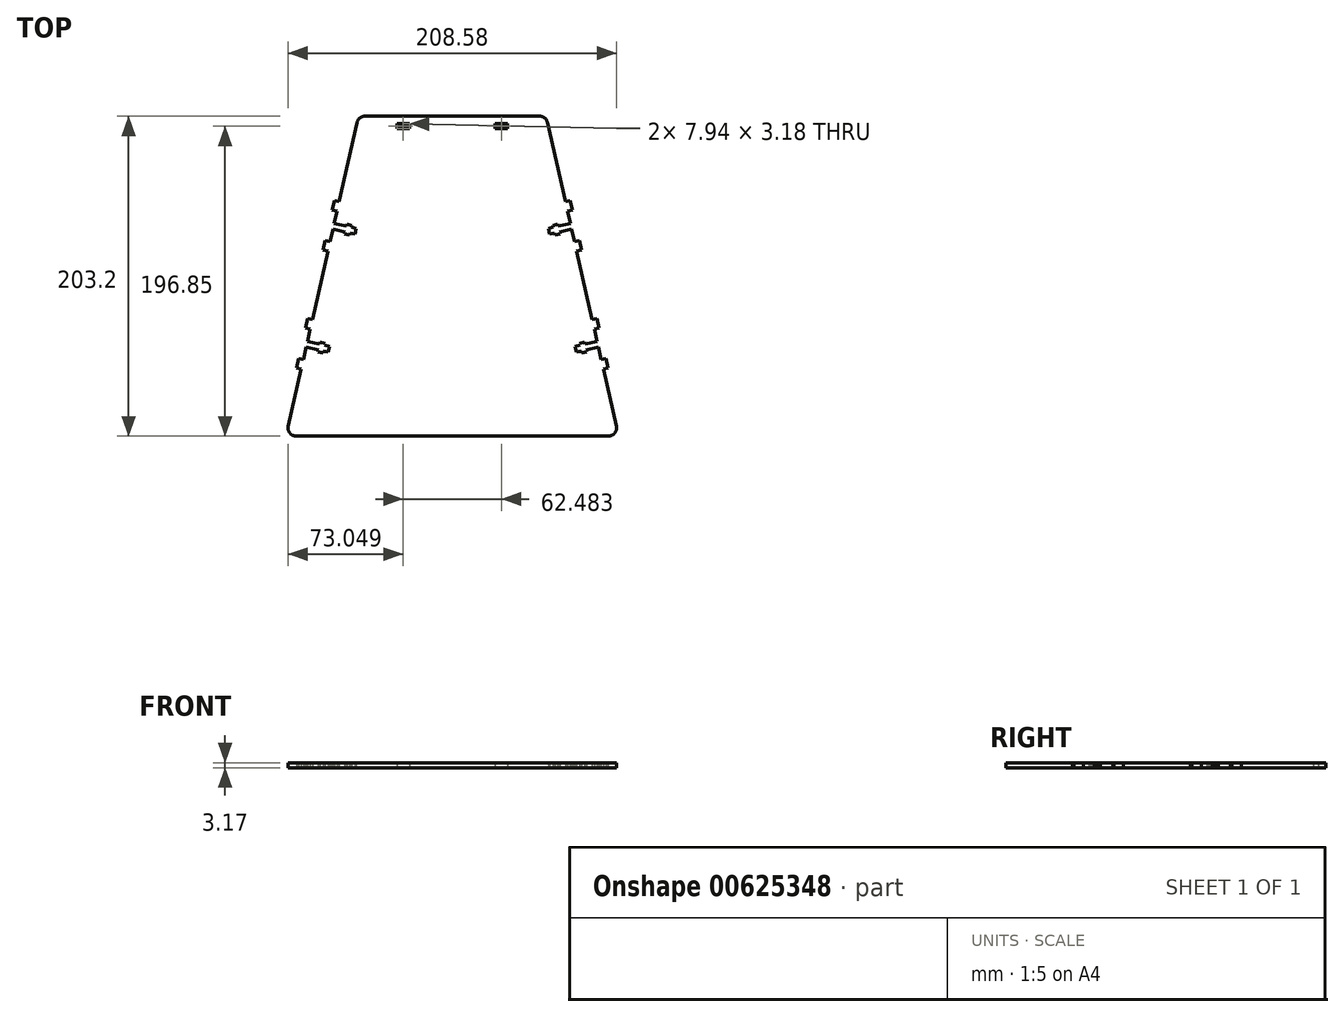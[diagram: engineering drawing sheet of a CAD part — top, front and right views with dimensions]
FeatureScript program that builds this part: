
annotation { "Feature Type Name" : "Feature", "Feature Type Description" : "" }
export const myFeature = defineFeature(function(context is Context, id is Id, definition is map)
    precondition{}
    {
        {
            var Q0;
            Q0=qCreatedBy(makeId("Top.planeOp"),FACE);
            var sketch = newSketch(context, id + "F0", { "sketchPlane" : qUnion([Q0])});
            skLineSegment(sketch, "E0", {"start": v(-59.53, 101.6) * mm, "end": v(59.53, 101.6) * mm});
            skLineSegment(sketch, "E1", {"start": v(-105.57, -101.6) * mm, "end": v(105.57, -101.6) * mm});
            skLineSegment(sketch, "E2", {"start": v(105.57, -101.6) * mm, "end": v(59.53, 101.6) * mm, "construction": true});
            skLineSegment(sketch, "E3", {"start": v(-59.53, 101.6) * mm, "end": v(-105.57, -101.6) * mm, "construction": true});
            skLineSegment(sketch, "E4", {"start": v(0, 0) * mm, "end": v(0, 101.6) * mm, "construction": true});
            skLineSegment(sketch, "E5.bottom", {"start": v(-27.27, 93.66) * mm, "end": v(-35.21, 93.66) * mm});
            skLineSegment(sketch, "E5.top", {"start": v(-27.27, 96.84) * mm, "end": v(-35.21, 96.84) * mm});
            skLineSegment(sketch, "E5.left", {"start": v(-27.27, 93.66) * mm, "end": v(-27.27, 96.84) * mm});
            skLineSegment(sketch, "E5.right", {"start": v(-35.21, 93.66) * mm, "end": v(-35.21, 96.84) * mm});
            skPoint(sketch, "E5.middle", {"position": v(-31.24, 95.25) * mm});
            skLineSegment(sketch, "E6", {"start": v(-35.21, 96.84) * mm, "end": v(-60.61, 96.84) * mm, "construction": true});
            skLineSegment(sketch, "E7", {"start": v(-59.53, 101.6) * mm, "end": v(-71.8, 47.41) * mm});
            skLineSegment(sketch, "E8", {"start": v(-71.8, 47.41) * mm, "end": v(-74.9, 48.11) * mm});
            skLineSegment(sketch, "E9", {"start": v(-74.9, 48.11) * mm, "end": v(-76.3, 41.92) * mm});
            skLineSegment(sketch, "E10", {"start": v(-76.3, 41.92) * mm, "end": v(-73.21, 41.22) * mm});
            skLineSegment(sketch, "E11", {"start": v(-73.21, 41.22) * mm, "end": v(-74.97, 33.48) * mm});
            skLineSegment(sketch, "E12", {"start": v(-74.97, 33.48) * mm, "end": v(-67.22, 31.72) * mm});
            skLineSegment(sketch, "E13", {"start": v(-67.22, 31.72) * mm, "end": v(-66.94, 32.96) * mm});
            skLineSegment(sketch, "E14", {"start": v(-66.94, 32.96) * mm, "end": v(-63.85, 32.26) * mm});
            skLineSegment(sketch, "E15", {"start": v(-63.85, 32.26) * mm, "end": v(-64.13, 31.02) * mm});
            skLineSegment(sketch, "E16", {"start": v(-64.13, 31.02) * mm, "end": v(-61.03, 30.32) * mm});
            skLineSegment(sketch, "E17", {"start": v(-61.03, 30.32) * mm, "end": v(-61.87, 26.6) * mm});
            skLineSegment(sketch, "E18", {"start": v(-61.87, 26.6) * mm, "end": v(-64.97, 27.3) * mm});
            skLineSegment(sketch, "E19", {"start": v(-64.97, 27.3) * mm, "end": v(-65.25, 26.07) * mm});
            skLineSegment(sketch, "E20", {"start": v(-65.25, 26.07) * mm, "end": v(-68.35, 26.77) * mm});
            skLineSegment(sketch, "E21", {"start": v(-68.35, 26.77) * mm, "end": v(-68.07, 28) * mm});
            skLineSegment(sketch, "E22", {"start": v(-68.07, 28) * mm, "end": v(-75.8, 29.76) * mm});
            skLineSegment(sketch, "E23", {"start": v(-75.8, 29.76) * mm, "end": v(-77.56, 22.02) * mm});
            skLineSegment(sketch, "E24", {"start": v(-77.56, 22.02) * mm, "end": v(-80.66, 22.72) * mm});
            skLineSegment(sketch, "E25", {"start": v(-80.66, 22.72) * mm, "end": v(-82.06, 16.53) * mm});
            skLineSegment(sketch, "E26", {"start": v(-82.06, 16.53) * mm, "end": v(-78.96, 15.83) * mm});
            skLineSegment(sketch, "E27", {"start": v(-78.96, 15.83) * mm, "end": v(-88.79, -27.52) * mm});
            skLineSegment(sketch, "E28", {"start": v(-83.88, -5.85) * mm, "end": v(0, -24.85) * mm, "construction": true});
            skLineSegment(sketch, "E29.MirrorCS", {"start": v(-85.04, -46.93) * mm, "end": v(-85.32, -48.17) * mm});
            skLineSegment(sketch, "E30.MirrorCS", {"start": v(-82.23, -48.87) * mm, "end": v(-81.95, -47.63) * mm});
            skLineSegment(sketch, "E31.MirrorCS", {"start": v(-81.1, -43.91) * mm, "end": v(-80.82, -42.68) * mm});
            skLineSegment(sketch, "E32.MirrorCS", {"start": v(-78, -44.62) * mm, "end": v(-81.1, -43.91) * mm});
            skLineSegment(sketch, "E33.MirrorCS", {"start": v(-85.32, -48.17) * mm, "end": v(-82.23, -48.87) * mm});
            skLineSegment(sketch, "E34.MirrorCS", {"start": v(-81.95, -47.63) * mm, "end": v(-78.85, -48.33) * mm});
            skLineSegment(sketch, "E35.MirrorCS", {"start": v(-91.88, -26.82) * mm, "end": v(-88.79, -27.52) * mm});
            skLineSegment(sketch, "E36.MirrorCS", {"start": v(-78.85, -48.33) * mm, "end": v(-78, -44.62) * mm});
            skLineSegment(sketch, "E37.MirrorCS", {"start": v(-80.82, -42.68) * mm, "end": v(-83.92, -41.97) * mm});
            skLineSegment(sketch, "E38.MirrorCS", {"start": v(-90.19, -33.72) * mm, "end": v(-93.29, -33.02) * mm});
            skLineSegment(sketch, "E39.MirrorCS", {"start": v(-93.29, -33.02) * mm, "end": v(-91.88, -26.82) * mm});
            skLineSegment(sketch, "E40.MirrorCS", {"start": v(-99.04, -58.4) * mm, "end": v(-97.64, -52.21) * mm});
            skLineSegment(sketch, "E41.MirrorCS", {"start": v(-95.94, -59.1) * mm, "end": v(-99.04, -58.4) * mm});
            skLineSegment(sketch, "E42.MirrorCS", {"start": v(-83.92, -41.97) * mm, "end": v(-84.2, -43.21) * mm});
            skLineSegment(sketch, "E43.MirrorCS", {"start": v(-97.64, -52.21) * mm, "end": v(-94.54, -52.92) * mm});
            skLineSegment(sketch, "E44.MirrorCS", {"start": v(-84.2, -43.21) * mm, "end": v(-91.94, -41.46) * mm});
            skLineSegment(sketch, "E45.MirrorCS", {"start": v(-91.94, -41.46) * mm, "end": v(-90.19, -33.72) * mm});
            skLineSegment(sketch, "E46.MirrorCS", {"start": v(-92.78, -45.18) * mm, "end": v(-85.04, -46.93) * mm});
            skLineSegment(sketch, "E47.MirrorCS", {"start": v(-94.54, -52.92) * mm, "end": v(-92.78, -45.18) * mm});
            skLineSegment(sketch, "E48", {"start": v(-95.94, -59.1) * mm, "end": v(-105.57, -101.6) * mm});
            skLineSegment(sketch, "E49.MirrorCS", {"start": v(64.13, 31.02) * mm, "end": v(61.03, 30.32) * mm});
            skLineSegment(sketch, "E50.MirrorCS", {"start": v(63.85, 32.26) * mm, "end": v(64.13, 31.02) * mm});
            skLineSegment(sketch, "E51.MirrorCS", {"start": v(68.35, 26.77) * mm, "end": v(68.07, 28) * mm});
            skLineSegment(sketch, "E52.MirrorCS", {"start": v(64.97, 27.3) * mm, "end": v(65.25, 26.07) * mm});
            skLineSegment(sketch, "E53.MirrorCS", {"start": v(66.94, 32.96) * mm, "end": v(63.85, 32.26) * mm});
            skLineSegment(sketch, "E54.MirrorCS", {"start": v(61.03, 30.32) * mm, "end": v(61.87, 26.6) * mm});
            skLineSegment(sketch, "E55.MirrorCS", {"start": v(67.22, 31.72) * mm, "end": v(66.94, 32.96) * mm});
            skLineSegment(sketch, "E56.MirrorCS", {"start": v(74.97, 33.48) * mm, "end": v(67.22, 31.72) * mm});
            skLineSegment(sketch, "E57.MirrorCS", {"start": v(68.07, 28) * mm, "end": v(75.8, 29.76) * mm});
            skLineSegment(sketch, "E58.MirrorCS", {"start": v(61.87, 26.6) * mm, "end": v(64.97, 27.3) * mm});
            skLineSegment(sketch, "E59.MirrorCS", {"start": v(65.25, 26.07) * mm, "end": v(68.35, 26.77) * mm});
            skLineSegment(sketch, "E60.MirrorCS", {"start": v(76.3, 41.92) * mm, "end": v(73.21, 41.22) * mm});
            skLineSegment(sketch, "E61.MirrorCS", {"start": v(73.21, 41.22) * mm, "end": v(74.97, 33.48) * mm});
            skLineSegment(sketch, "E62.MirrorCS", {"start": v(27.27, 96.84) * mm, "end": v(35.21, 96.84) * mm});
            skLineSegment(sketch, "E63.MirrorCS", {"start": v(35.21, 93.66) * mm, "end": v(35.21, 96.84) * mm});
            skLineSegment(sketch, "E64.MirrorCS", {"start": v(71.8, 47.41) * mm, "end": v(74.9, 48.11) * mm});
            skLineSegment(sketch, "E65.MirrorCS", {"start": v(74.9, 48.11) * mm, "end": v(76.3, 41.92) * mm});
            skLineSegment(sketch, "E66.MirrorCS", {"start": v(75.8, 29.76) * mm, "end": v(77.56, 22.02) * mm});
            skLineSegment(sketch, "E67.MirrorCS", {"start": v(27.27, 93.66) * mm, "end": v(35.21, 93.66) * mm});
            skLineSegment(sketch, "E68.MirrorCS", {"start": v(27.27, 93.66) * mm, "end": v(27.27, 96.84) * mm});
            skLineSegment(sketch, "E69.MirrorCS", {"start": v(80.66, 22.72) * mm, "end": v(82.06, 16.53) * mm});
            skLineSegment(sketch, "E70.MirrorCS", {"start": v(77.56, 22.02) * mm, "end": v(80.66, 22.72) * mm});
            skLineSegment(sketch, "E71.MirrorCS", {"start": v(82.06, 16.53) * mm, "end": v(78.96, 15.83) * mm});
            skPoint(sketch, "E72.MirrorP", {"position": v(31.24, 95.25) * mm});
            skLineSegment(sketch, "E73.MirrorCS", {"start": v(35.21, 96.84) * mm, "end": v(60.61, 96.84) * mm, "construction": true});
            skLineSegment(sketch, "E74.MirrorCS", {"start": v(59.53, 101.6) * mm, "end": v(71.8, 47.41) * mm});
            skLineSegment(sketch, "E75.MirrorCS", {"start": v(81.1, -43.91) * mm, "end": v(80.82, -42.68) * mm});
            skLineSegment(sketch, "E76.MirrorCS", {"start": v(82.23, -48.87) * mm, "end": v(81.95, -47.63) * mm});
            skLineSegment(sketch, "E77.MirrorCS", {"start": v(81.95, -47.63) * mm, "end": v(78.85, -48.33) * mm});
            skLineSegment(sketch, "E78.MirrorCS", {"start": v(80.82, -42.68) * mm, "end": v(83.92, -41.97) * mm});
            skLineSegment(sketch, "E79.MirrorCS", {"start": v(85.04, -46.93) * mm, "end": v(85.32, -48.17) * mm});
            skLineSegment(sketch, "E80.MirrorCS", {"start": v(85.32, -48.17) * mm, "end": v(82.23, -48.87) * mm});
            skLineSegment(sketch, "E81.MirrorCS", {"start": v(83.92, -41.97) * mm, "end": v(84.2, -43.21) * mm});
            skLineSegment(sketch, "E82.MirrorCS", {"start": v(78, -44.62) * mm, "end": v(81.1, -43.91) * mm});
            skLineSegment(sketch, "E83.MirrorCS", {"start": v(78.85, -48.33) * mm, "end": v(78, -44.62) * mm});
            skLineSegment(sketch, "E84.MirrorCS", {"start": v(94.54, -52.92) * mm, "end": v(92.78, -45.18) * mm});
            skLineSegment(sketch, "E85.MirrorCS", {"start": v(91.88, -26.82) * mm, "end": v(88.79, -27.52) * mm});
            skLineSegment(sketch, "E86.MirrorCS", {"start": v(84.2, -43.21) * mm, "end": v(91.94, -41.46) * mm});
            skLineSegment(sketch, "E87.MirrorCS", {"start": v(90.19, -33.72) * mm, "end": v(93.29, -33.02) * mm});
            skLineSegment(sketch, "E88.MirrorCS", {"start": v(92.78, -45.18) * mm, "end": v(85.04, -46.93) * mm});
            skLineSegment(sketch, "E89.MirrorCS", {"start": v(97.64, -52.21) * mm, "end": v(94.54, -52.92) * mm});
            skLineSegment(sketch, "E90.MirrorCS", {"start": v(95.94, -59.1) * mm, "end": v(99.04, -58.4) * mm});
            skLineSegment(sketch, "E91.MirrorCS", {"start": v(91.94, -41.46) * mm, "end": v(90.19, -33.72) * mm});
            skLineSegment(sketch, "E92.MirrorCS", {"start": v(93.29, -33.02) * mm, "end": v(91.88, -26.82) * mm});
            skLineSegment(sketch, "E93.MirrorCS", {"start": v(99.04, -58.4) * mm, "end": v(97.64, -52.21) * mm});
            skLineSegment(sketch, "E94", {"start": v(78.96, 15.83) * mm, "end": v(88.79, -27.52) * mm});
            skLineSegment(sketch, "E95", {"start": v(95.94, -59.1) * mm, "end": v(105.57, -101.6) * mm});
            skSolve(sketch);
        }
        {
            var Q0;
            Q0 = qSketchRegion(id + "F0", true);
            extrude(context, id + "F1", {"entities" : qUnion([Q0]), "depth" : 3.17 * mm, "offsetDistance" : 25.4 * mm});
        }
        {
            var Q0;
            Q0=makeQuery(id+"F1.opExtrude","SWEPT_EDGE",EDGE,{"disambiguationData":[OSD([sQuery(id+"F0.wireOp",EDGE,"E0"),sQuery(id+"F0.wireOp",EDGE,"E7")])]});
            var Q1;
            Q1=makeQuery(id+"F1.opExtrude","SWEPT_EDGE",EDGE,{"disambiguationData":[OSD([sQuery(id+"F0.wireOp",EDGE,"E0"),sQuery(id+"F0.wireOp",EDGE,"E74.MirrorCS")])]});
            var Q2;
            Q2=makeQuery(id+"F1.opExtrude","SWEPT_EDGE",EDGE,{"disambiguationData":[OSD([sQuery(id+"F0.wireOp",EDGE,"E1"),sQuery(id+"F0.wireOp",EDGE,"E95")])]});
            var Q3;
            Q3=makeQuery(id+"F1.opExtrude","SWEPT_EDGE",EDGE,{"disambiguationData":[OSD([sQuery(id+"F0.wireOp",EDGE,"E1"),sQuery(id+"F0.wireOp",EDGE,"E48")])]});
            fillet(context, id + "F2", {"entities" : qUnion([Q0, Q1, Q2, Q3]), "radius" : 5.08 * mm, "tangentPropagation" : true, "allowEdgeOverflow" : false});
        }
    });
